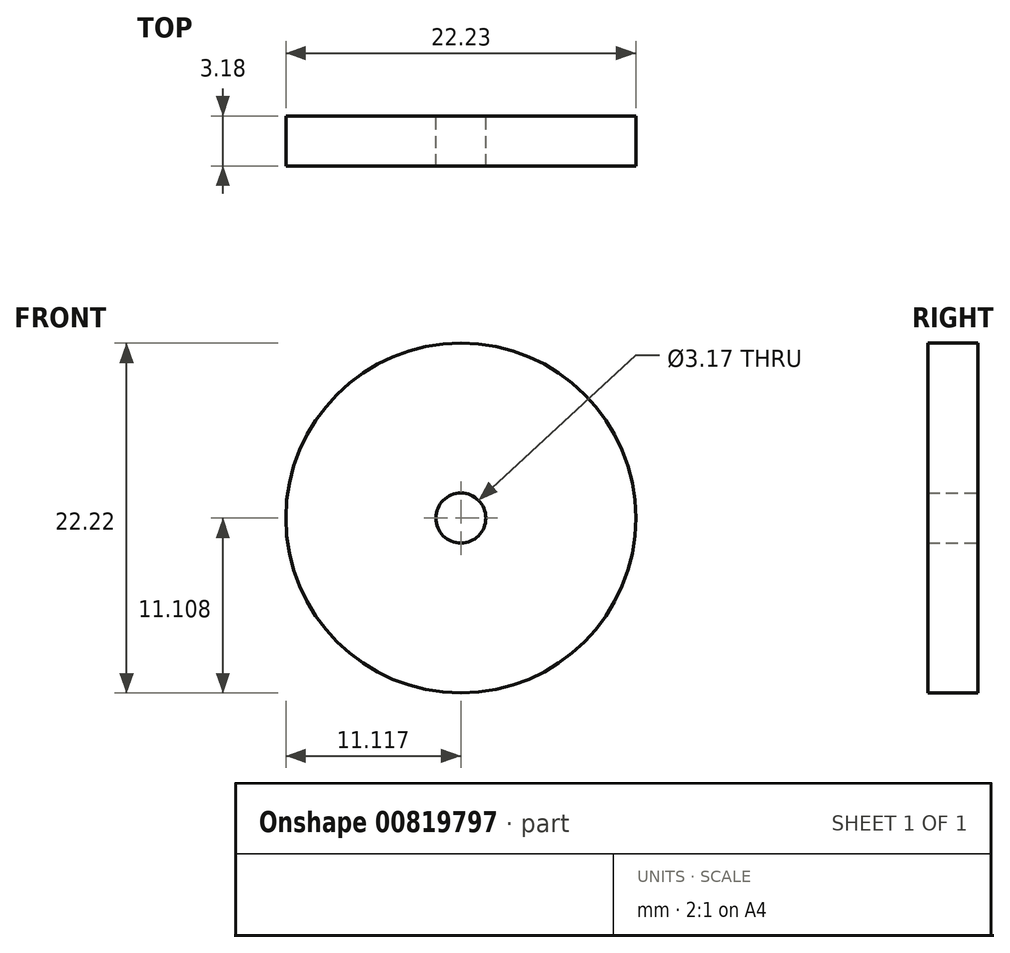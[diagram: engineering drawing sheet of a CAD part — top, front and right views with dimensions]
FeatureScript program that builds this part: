
annotation { "Feature Type Name" : "Feature", "Feature Type Description" : "" }
export const myFeature = defineFeature(function(context is Context, id is Id, definition is map)
    precondition{}
    {
        {
            var Q0;
            Q0=qCreatedBy(makeId("Front.planeOp"),FACE);
            var sketch = newSketch(context, id + "F0", { "sketchPlane" : qUnion([Q0])});
            skCircle(sketch, "E0", {"center": v(-66.07, 48.97) * mm, "radius": 11.11 * mm});
            skCircle(sketch, "E1", {"center": v(-66.07, 48.97) * mm, "radius": 1.59 * mm});
            skSolve(sketch);
        }
        {
            var Q0;
            Q0=makeQuery(id+"F0.imprint","IMPRINT",FACE,{"disambiguationData":[TD([[makeQuery(id+"F0.imprint","IMPRINT",EDGE,{"derivedFrom":sQuery(id+"F0.wireOp",EDGE,"E0")}),1.0]])]});
            extrude(context, id + "F1", {"entities" : qUnion([Q0]), "depth" : 3.17 * mm, "offsetDistance" : 25.4 * mm});
        }
    });
